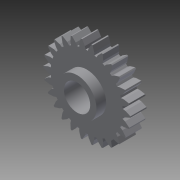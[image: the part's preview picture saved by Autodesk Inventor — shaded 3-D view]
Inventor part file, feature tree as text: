
AUTODESK INVENTOR PART (.ipt)
format: ipt  version: 2015 SP1 (Build 190203100, 203)  size: 236,544 bytes
history: native  units: mm
features: extrude x4, sketch x3, pattern_circular x1
ambient origin geometry x8: Origin, YZ Plane, XZ Plane, XY Plane, X Axis, Y Axis, Z Axis, Center Point
bodies: Solid1 (feature_tree)
feature tree (8):
  sketch  "Sketch1"  dims[d0=27.0mm d2=24.003mm]
  extrude  "Extrusion1"  Depth=24.003mm
  extrude  "Extrusion2"  Depth=0.375mm
  pattern_circular  "Circular Pattern1"  [2 undecoded]
  extrude  "Extrusion3"  Depth=3.0mm
  extrude  "Extrusion4"  Depth=5.0mm TaperAngle=0.0deg
  sketch  "Sketch2"  dims[d3=2.0mm d4=0.375mm]
  sketch  "Sketch3"  dims[d5=1.75mm d6=5.0mm d7=0.0mm d8=22.352mm d9=5.0mm d10=0.0mm d11=260.0mm d12=360.0deg d14=8.125mm d15=5.0mm d16=0.0mm d17=12.0mm d18=3.0mm d19=0.0mm]
note: 2 required parameter values undecoded (feature->parameter linkage not recoverable at this tier; creation-order binding heuristic only, values carry confidence <= 0.55)
